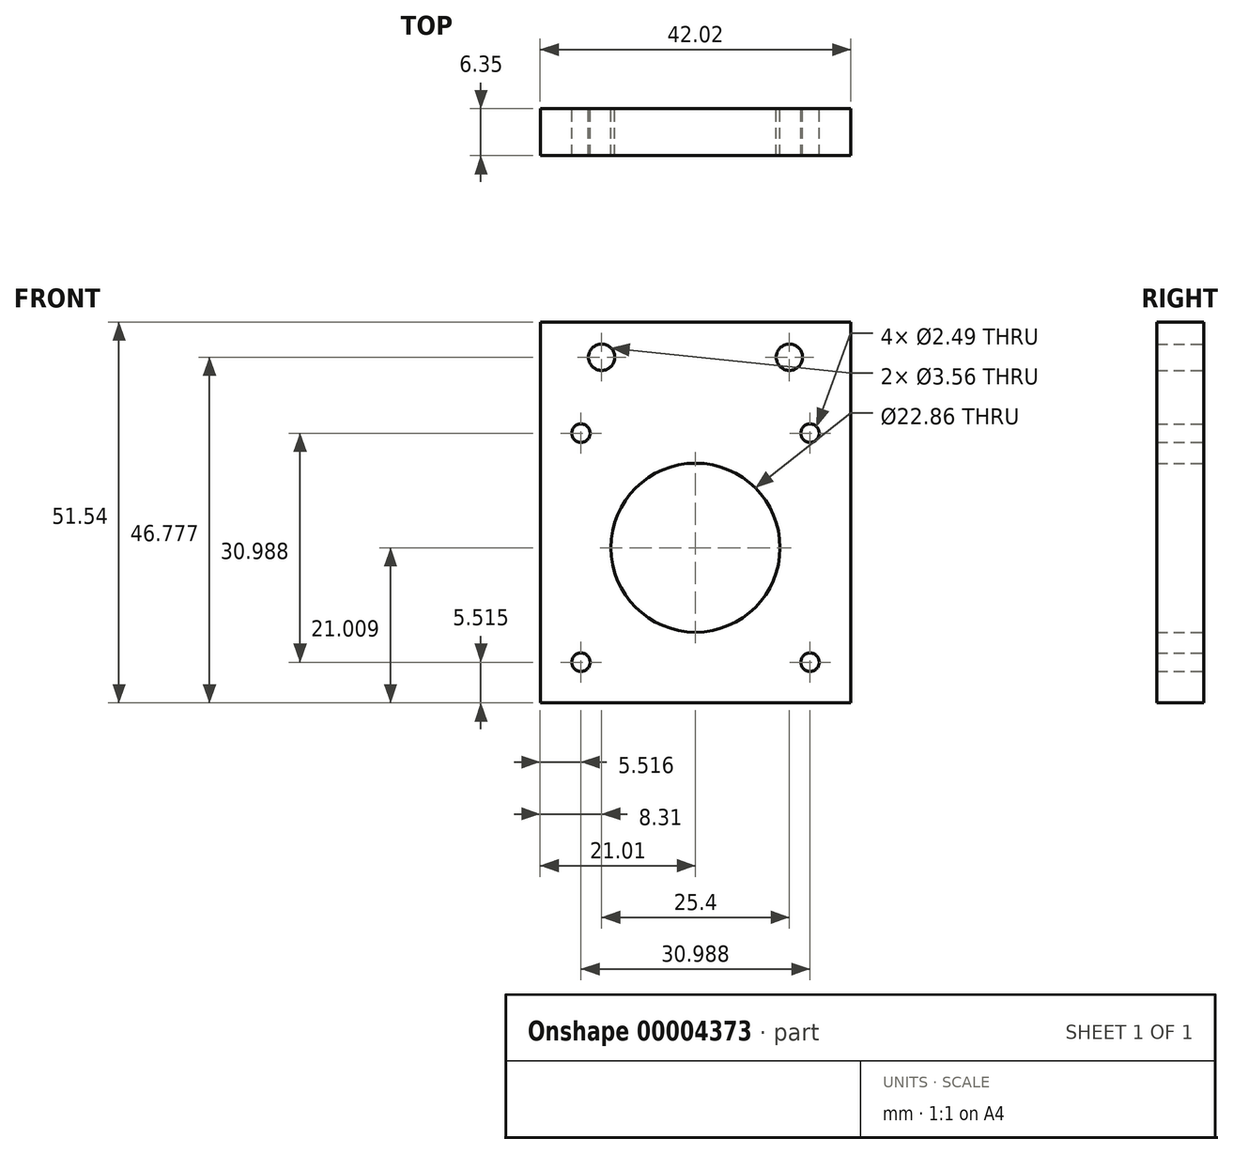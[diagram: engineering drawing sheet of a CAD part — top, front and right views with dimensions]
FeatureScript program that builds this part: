
annotation { "Feature Type Name" : "Feature", "Feature Type Description" : "" }
export const myFeature = defineFeature(function(context is Context, id is Id, definition is map)
    precondition{}
    {
        {
            var Q0;
            Q0=qCreatedBy(makeId("Front.planeOp"),FACE);
            var sketch = newSketch(context, id + "F0", { "sketchPlane" : qUnion([Q0])});
            skLineSegment(sketch, "E0.bottom", {"start": v(-21, 0) * mm, "end": v(21, 0) * mm});
            skLineSegment(sketch, "E0.top", {"start": v(-21, -51.54) * mm, "end": v(21, -51.54) * mm});
            skLineSegment(sketch, "E0.left", {"start": v(-21, 0) * mm, "end": v(-21, -51.54) * mm});
            skLineSegment(sketch, "E0.right", {"start": v(21, 0) * mm, "end": v(21, -51.54) * mm});
            skLineSegment(sketch, "E1", {"start": v(-21, -9.53) * mm, "end": v(21, -9.53) * mm, "construction": true});
            skLineSegment(sketch, "E2.rect.bottom", {"start": v(15.5, -15.04) * mm, "end": v(-15.5, -15.04) * mm, "construction": true});
            skLineSegment(sketch, "E2.rect.top", {"start": v(15.5, -46.02) * mm, "end": v(-15.5, -46.02) * mm, "construction": true});
            skLineSegment(sketch, "E2.rect.left", {"start": v(15.5, -15.04) * mm, "end": v(15.5, -46.02) * mm, "construction": true});
            skLineSegment(sketch, "E2.rect.right", {"start": v(-15.5, -15.04) * mm, "end": v(-15.5, -46.02) * mm, "construction": true});
            skPoint(sketch, "E2.rect.middle", {"position": v(0, -30.53) * mm});
            skLineSegment(sketch, "E3", {"start": v(0, -9.53) * mm, "end": v(0, -51.54) * mm, "construction": true});
            skCircle(sketch, "E4", {"center": v(15.5, -15.04) * mm, "radius": 1.24 * mm});
            skCircle(sketch, "E5", {"center": v(-15.5, -15.04) * mm, "radius": 1.24 * mm});
            skCircle(sketch, "E6", {"center": v(-15.5, -46.02) * mm, "radius": 1.24 * mm});
            skCircle(sketch, "E7", {"center": v(15.5, -46.02) * mm, "radius": 1.24 * mm});
            skLineSegment(sketch, "E8", {"start": v(-21, -4.76) * mm, "end": v(21, -4.76) * mm, "construction": true});
            skLineSegment(sketch, "E9", {"start": v(0, 0) * mm, "end": v(0, -9.53) * mm, "construction": true});
            skPoint(sketch, "E10", {"position": v(0, -4.76) * mm});
            skCircle(sketch, "E11", {"center": v(12.7, -4.76) * mm, "radius": 1.78 * mm});
            skCircle(sketch, "E12.0.MirrorC", {"center": v(-12.7, -4.76) * mm, "radius": 1.78 * mm});
            skCircle(sketch, "E13", {"center": v(0, -30.53) * mm, "radius": 11.43 * mm});
            skSolve(sketch);
        }
        {
            var Q0;
            Q0=makeQuery(id+"F0.imprint","IMPRINT",FACE,{"disambiguationData":[TD([[makeQuery(id+"F0.imprint","IMPRINT",EDGE,{"derivedFrom":sQuery(id+"F0.wireOp",EDGE,"E0.bottom")}),-1.0]])]});
            extrude(context, id + "F1", {"entities" : qUnion([Q0]), "depth" : 6.35 * mm});
        }
    });
